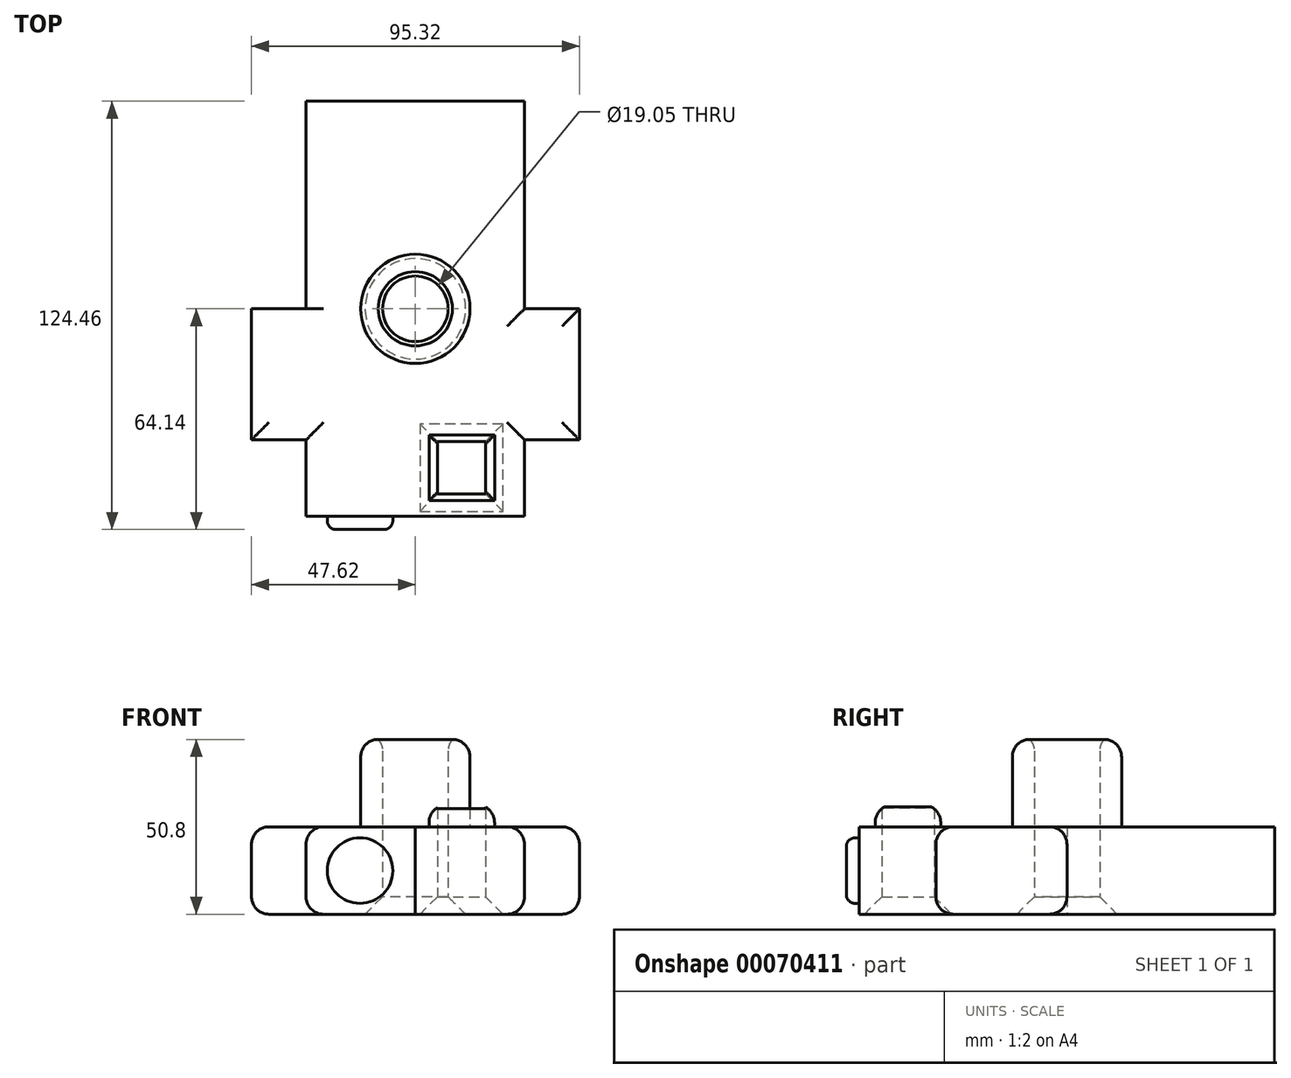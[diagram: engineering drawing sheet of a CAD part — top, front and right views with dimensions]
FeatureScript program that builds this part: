
annotation { "Feature Type Name" : "Feature", "Feature Type Description" : "" }
export const myFeature = defineFeature(function(context is Context, id is Id, definition is map)
    precondition{}
    {
        {
            var Q0;
            Q0=qCreatedBy(makeId("Top.planeOp"),FACE);
            var sketch = newSketch(context, id + "F0", { "sketchPlane" : qUnion([Q0])});
            skCircle(sketch, "E0", {"center": v(0, 0) * mm, "radius": 15.88 * mm});
            skLineSegment(sketch, "E1.bottom", {"start": v(0, 60.33) * mm, "end": v(31.75, 60.33) * mm});
            skLineSegment(sketch, "E1.top", {"start": v(0, -60.34) * mm, "end": v(31.75, -60.34) * mm});
            skLineSegment(sketch, "E1.right", {"start": v(31.75, 60.33) * mm, "end": v(31.75, 0) * mm});
            skLineSegment(sketch, "E2.bottom", {"start": v(0, 60.33) * mm, "end": v(-31.75, 60.33) * mm});
            skLineSegment(sketch, "E2.top", {"start": v(0, -60.33) * mm, "end": v(-31.75, -60.33) * mm});
            skLineSegment(sketch, "E2.right", {"start": v(-31.75, 60.33) * mm, "end": v(-31.75, 0) * mm});
            skLineSegment(sketch, "E3", {"start": v(31.75, 0) * mm, "end": v(47.62, 0) * mm});
            skLineSegment(sketch, "E4", {"start": v(-31.75, 0) * mm, "end": v(-47.62, 0) * mm});
            skLineSegment(sketch, "E5.bottom", {"start": v(31.75, 0) * mm, "end": v(47.7, 0) * mm});
            skLineSegment(sketch, "E5.top", {"start": v(31.75, -38.1) * mm, "end": v(47.7, -38.1) * mm});
            skLineSegment(sketch, "E5.right", {"start": v(47.7, 0) * mm, "end": v(47.7, -38.1) * mm});
            skLineSegment(sketch, "E6.bottom", {"start": v(-47.62, 0) * mm, "end": v(-31.75, 0) * mm});
            skLineSegment(sketch, "E6.top", {"start": v(-47.62, -38.1) * mm, "end": v(-31.75, -38.1) * mm});
            skLineSegment(sketch, "E6.left", {"start": v(-47.62, 0) * mm, "end": v(-47.62, -38.1) * mm});
            skPoint(sketch, "E7.orphan", {"position": v(15.88, 0) * mm});
            skPoint(sketch, "E8.orphan", {"position": v(-15.88, 0) * mm});
            skLineSegment(sketch, "E9.trimOffspring", {"start": v(-31.75, -38.1) * mm, "end": v(-31.75, -60.33) * mm});
            skLineSegment(sketch, "E10.trimOffspring", {"start": v(31.75, -38.1) * mm, "end": v(31.75, -60.34) * mm});
            skLineSegment(sketch, "E11.trimOffspring", {"start": v(0, -60.33) * mm, "end": v(0, -60.34) * mm});
            skPoint(sketch, "E12.end.orphan", {"position": v(0, -60.33) * mm});
            skPoint(sketch, "E13.orphan", {"position": v(0, -15.88) * mm});
            skPoint(sketch, "E14.start.orphan", {"position": v(0, 15.88) * mm});
            skCircle(sketch, "E15", {"center": v(0, 0) * mm, "radius": 9.53 * mm});
            skLineSegment(sketch, "E16.bottom", {"start": v(3.98, -36.68) * mm, "end": v(23.03, -36.68) * mm});
            skLineSegment(sketch, "E16.top", {"start": v(3.98, -55.73) * mm, "end": v(23.03, -55.73) * mm});
            skLineSegment(sketch, "E16.left", {"start": v(3.98, -36.68) * mm, "end": v(3.98, -55.73) * mm});
            skLineSegment(sketch, "E16.right", {"start": v(23.03, -36.68) * mm, "end": v(23.03, -55.73) * mm});
            skLineSegment(sketch, "E17.bottom", {"start": v(6.4, -38.54) * mm, "end": v(20.37, -38.54) * mm});
            skLineSegment(sketch, "E17.top", {"start": v(6.4, -53.78) * mm, "end": v(20.37, -53.78) * mm});
            skLineSegment(sketch, "E17.left", {"start": v(6.4, -38.54) * mm, "end": v(6.4, -53.78) * mm});
            skLineSegment(sketch, "E17.right", {"start": v(20.37, -38.54) * mm, "end": v(20.37, -53.78) * mm});
            skSolve(sketch);
        }
        {
            var Q0;
            Q0=makeQuery(id+"F0.imprint","IMPRINT",FACE,{"disambiguationData":[TD([[makeQuery(id+"F0.imprint","IMPRINT",EDGE,{"derivedFrom":sQuery(id+"F0.wireOp",EDGE,"E0")}),-1.0]])]});
            extrude(context, id + "F1", {"entities" : qUnion([Q0]), "depth" : 25.4 * mm});
        }
        {
            var Q0;
            Q0=makeQuery(id+"F0.imprint","IMPRINT",FACE,{"disambiguationData":[TD([[makeQuery(id+"F0.imprint","IMPRINT",EDGE,{"derivedFrom":sQuery(id+"F0.wireOp",EDGE,"E0")}),1.0]])]});
            extrude(context, id + "F2", {"entities" : qUnion([Q0]), "operationType" : NewBodyOperationType.ADD, "depth" : 50.8 * mm});
        }
        {
            var Q0;
            Q0=makeQuery(id+"F0.imprint","IMPRINT",FACE,{"disambiguationData":[TD([[makeQuery(id+"F0.imprint","IMPRINT",EDGE,{"derivedFrom":sQuery(id+"F0.wireOp",EDGE,"E16.bottom")}),-1.0]])]});
            extrude(context, id + "F3", {"entities" : qUnion([Q0]), "operationType" : NewBodyOperationType.ADD, "depth" : 31.75 * mm});
        }
        {
            var Q0;
            Q0=makeQuery(id+"F1.opExtrude","SWEPT_FACE",FACE,{"disambiguationData":[OSD([sQuery(id+"F0.wireOp",EDGE,"E2.top")])]});
            var sketch = newSketch(context, id + "F4", { "sketchPlane" : qUnion([Q0])});
            skCircle(sketch, "E18", {"center": v(-16.08, 12.67) * mm, "radius": 9.53 * mm});
            skSolve(sketch);
        }
        {
            var Q0;
            Q0=makeQuery(id+"F4.imprint","IMPRINT",FACE,{"disambiguationData":[TD([[makeQuery(id+"F4.imprint","IMPRINT",EDGE,{"derivedFrom":sQuery(id+"F4.wireOp",EDGE,"E18")}),1.0]])]});
            extrude(context, id + "F5", {"entities" : qUnion([Q0]), "operationType" : NewBodyOperationType.ADD, "depth" : 3.8 * mm});
        }
        {
            var Q0;
            Q0=makeQuery(id+"F5.opExtrude","CAP_EDGE",EDGE,{"disambiguationData":[OSD([sQuery(id+"F4.wireOp",EDGE,"E18")])],"isStart":false});
            fillet(context, id + "F6", {"entities" : qUnion([Q0]), "radius" : 2.54 * mm, "tangentPropagation" : true, "allowEdgeOverflow" : false});
        }
        {
            var Q0;
            Q0=makeQuery(id+"F2.opExtrude","CAP_EDGE",EDGE,{"disambiguationData":[OSD([sQuery(id+"F0.wireOp",EDGE,"E0")])],"isStart":false});
            fillet(context, id + "F7", {"entities" : qUnion([Q0]), "radius" : 5.08 * mm, "tangentPropagation" : true, "allowEdgeOverflow" : false});
        }
        {
            var Q0;
            Q0=makeQuery(id+"F2.opExtrude","CAP_EDGE",EDGE,{"disambiguationData":[OSD([sQuery(id+"F0.wireOp",EDGE,"E15")])],"isStart":false});
            fillet(context, id + "F8", {"entities" : qUnion([Q0]), "radius" : 5.08 * mm, "tangentPropagation" : true, "allowEdgeOverflow" : false});
        }
        {
            var Q0;
            Q0=makeQuery(id+"F3.opExtrude","CAP_EDGE",EDGE,{"disambiguationData":[OSD([sQuery(id+"F0.wireOp",EDGE,"E16.left")])],"isStart":false});
            var Q1;
            Q1=makeQuery(id+"F3.opExtrude","CAP_EDGE",EDGE,{"disambiguationData":[OSD([sQuery(id+"F0.wireOp",EDGE,"E16.right")])],"isStart":false});
            var Q2;
            Q2=makeQuery(id+"F3.opExtrude","CAP_EDGE",EDGE,{"disambiguationData":[OSD([sQuery(id+"F0.wireOp",EDGE,"E16.bottom")])],"isStart":false});
            var Q3;
            Q3=makeQuery(id+"F3.opExtrude","CAP_EDGE",EDGE,{"disambiguationData":[OSD([sQuery(id+"F0.wireOp",EDGE,"E16.top")])],"isStart":false});
            fillet(context, id + "F9", {"entities" : qUnion([Q0, Q1, Q2, Q3]), "radius" : 5.08 * mm, "tangentPropagation" : true, "allowEdgeOverflow" : false});
        }
        {
            var Q0;
            Q0=makeQuery(id+"F1.opExtrude","CAP_EDGE",EDGE,{"disambiguationData":[OSD([sQuery(id+"F0.wireOp",EDGE,"E5.top")])],"isStart":false});
            var Q1;
            Q1=makeQuery(id+"F1.opExtrude","CAP_EDGE",EDGE,{"disambiguationData":[OSD([sQuery(id+"F0.wireOp",EDGE,"E10.trimOffspring")])],"isStart":false});
            var Q2;
            Q2=makeQuery(id+"F1.opExtrude","CAP_EDGE",EDGE,{"disambiguationData":[OSD([sQuery(id+"F0.wireOp",EDGE,"E9.trimOffspring")])],"isStart":false});
            var Q3;
            Q3=makeQuery(id+"F1.opExtrude","CAP_EDGE",EDGE,{"disambiguationData":[OSD([sQuery(id+"F0.wireOp",EDGE,"E6.top")])],"isStart":false});
            var Q4;
            Q4=makeQuery(id+"F1.opExtrude","CAP_EDGE",EDGE,{"disambiguationData":[OSD([sQuery(id+"F0.wireOp",EDGE,"E2.right")])],"isStart":false});
            var Q5;
            Q5=makeQuery(id+"F1.opExtrude","CAP_EDGE",EDGE,{"disambiguationData":[OSD([sQuery(id+"F0.wireOp",EDGE,"E6.bottom")])],"isStart":false});
            var Q6;
            Q6=makeQuery(id+"F1.opExtrude","CAP_EDGE",EDGE,{"disambiguationData":[OSD([sQuery(id+"F0.wireOp",EDGE,"E5.bottom")])],"isStart":false});
            var Q7;
            Q7=makeQuery(id+"F1.opExtrude","CAP_EDGE",EDGE,{"disambiguationData":[OSD([sQuery(id+"F0.wireOp",EDGE,"E1.right")])],"isStart":false});
            var Q8;
            Q8=makeQuery(id+"F1.opExtrude","CAP_EDGE",EDGE,{"disambiguationData":[OSD([sQuery(id+"F0.wireOp",EDGE,"E9.trimOffspring")])],"isStart":true});
            var Q9;
            Q9=makeQuery(id+"F1.opExtrude","CAP_EDGE",EDGE,{"disambiguationData":[OSD([sQuery(id+"F0.wireOp",EDGE,"E2.right")])],"isStart":true});
            var Q10;
            Q10=makeQuery(id+"F1.opExtrude","CAP_EDGE",EDGE,{"disambiguationData":[OSD([sQuery(id+"F0.wireOp",EDGE,"E6.bottom")])],"isStart":true});
            var Q11;
            Q11=makeQuery(id+"F1.opExtrude","CAP_EDGE",EDGE,{"disambiguationData":[OSD([sQuery(id+"F0.wireOp",EDGE,"E6.top")])],"isStart":true});
            var Q12;
            Q12=makeQuery(id+"F1.opExtrude","CAP_EDGE",EDGE,{"disambiguationData":[OSD([sQuery(id+"F0.wireOp",EDGE,"E6.left")])],"isStart":true});
            var Q13;
            Q13=makeQuery(id+"F1.opExtrude","CAP_EDGE",EDGE,{"disambiguationData":[OSD([sQuery(id+"F0.wireOp",EDGE,"E1.right")])],"isStart":true});
            var Q14;
            Q14=makeQuery(id+"F1.opExtrude","CAP_EDGE",EDGE,{"disambiguationData":[OSD([sQuery(id+"F0.wireOp",EDGE,"E10.trimOffspring")])],"isStart":true});
            var Q15;
            Q15=makeQuery(id+"F1.opExtrude","CAP_EDGE",EDGE,{"disambiguationData":[OSD([sQuery(id+"F0.wireOp",EDGE,"E5.top")])],"isStart":true});
            var Q16;
            Q16=makeQuery(id+"F1.opExtrude","CAP_EDGE",EDGE,{"disambiguationData":[OSD([sQuery(id+"F0.wireOp",EDGE,"E5.right")])],"isStart":true});
            var Q17;
            Q17=makeQuery(id+"F1.opExtrude","CAP_EDGE",EDGE,{"disambiguationData":[OSD([sQuery(id+"F0.wireOp",EDGE,"E5.bottom")])],"isStart":true});
            var Q18;
            Q18=makeQuery(id+"F1.opExtrude","CAP_EDGE",EDGE,{"disambiguationData":[OSD([sQuery(id+"F0.wireOp",EDGE,"E5.right")])],"isStart":false});
            var Q19;
            Q19=makeQuery(id+"F1.opExtrude","CAP_EDGE",EDGE,{"disambiguationData":[OSD([sQuery(id+"F0.wireOp",EDGE,"E6.left")])],"isStart":false});
            fillet(context, id + "F10", {"entities" : qUnion([Q0, Q1, Q2, Q3, Q4, Q5, Q6, Q7, Q8, Q9, Q10, Q11, Q12, Q13, Q14, Q15, Q16, Q17, Q18, Q19]), "radius" : 5.08 * mm, "tangentPropagation" : true, "allowEdgeOverflow" : false});
        }
        {
            var Q0;
            Q0=makeQuery(id+"F3.opExtrude","CAP_EDGE",EDGE,{"disambiguationData":[OSD([sQuery(id+"F0.wireOp",EDGE,"E17.bottom")])],"isStart":true});
            var Q1;
            Q1=makeQuery(id+"F3.opExtrude","CAP_EDGE",EDGE,{"disambiguationData":[OSD([sQuery(id+"F0.wireOp",EDGE,"E17.right")])],"isStart":true});
            var Q2;
            Q2=makeQuery(id+"F3.opExtrude","CAP_EDGE",EDGE,{"disambiguationData":[OSD([sQuery(id+"F0.wireOp",EDGE,"E17.top")])],"isStart":true});
            var Q3;
            Q3=makeQuery(id+"F3.opExtrude","CAP_EDGE",EDGE,{"disambiguationData":[OSD([sQuery(id+"F0.wireOp",EDGE,"E17.left")])],"isStart":true});
            chamfer(context, id + "F11", {"entities" : qUnion([Q0, Q1, Q2, Q3]), "width" : 5.08 * mm, "tangentPropagation" : true});
        }
        {
            var Q0;
            Q0=makeQuery(id+"F2.opExtrude","CAP_EDGE",EDGE,{"disambiguationData":[OSD([sQuery(id+"F0.wireOp",EDGE,"E15")])],"isStart":true});
            chamfer(context, id + "F12", {"entities" : qUnion([Q0]), "width" : 5.08 * mm, "tangentPropagation" : true});
        }
    });
